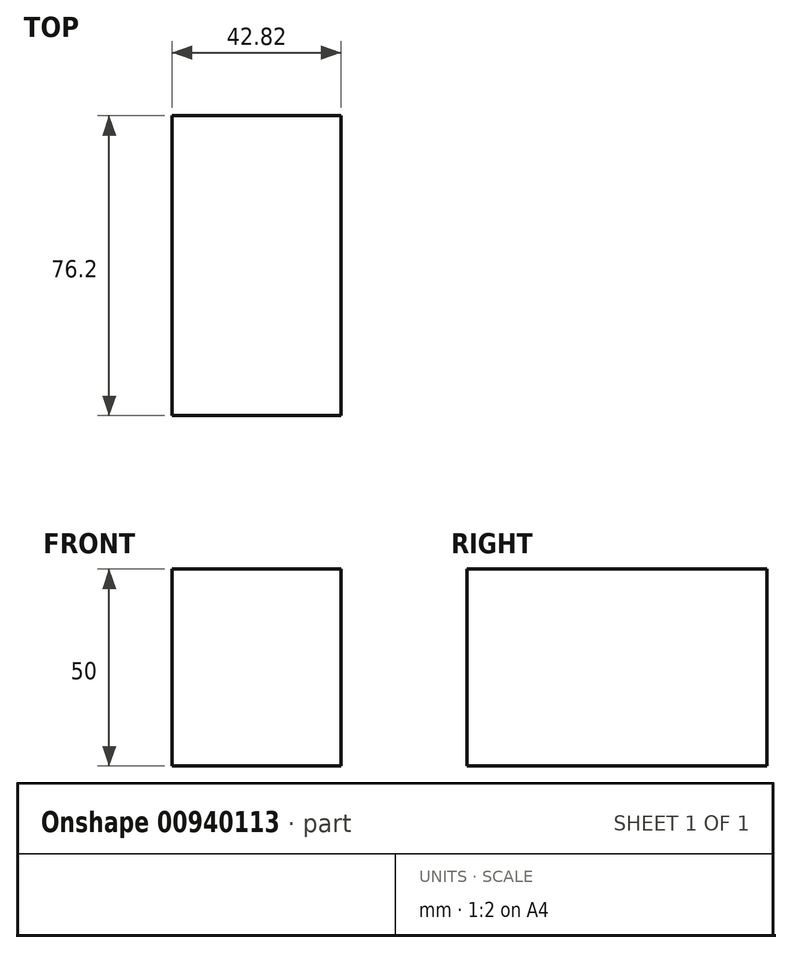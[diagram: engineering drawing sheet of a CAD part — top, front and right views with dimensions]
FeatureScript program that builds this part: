
annotation { "Feature Type Name" : "Feature", "Feature Type Description" : "" }
export const myFeature = defineFeature(function(context is Context, id is Id, definition is map)
    precondition{}
    {
        {
            var Q0;
            Q0=qCreatedBy(makeId("Front.planeOp"),FACE);
            var sketch = newSketch(context, id + "F0", { "sketchPlane" : qUnion([Q0])});
            skLineSegment(sketch, "E0.bottom", {"start": v(21.4, 25) * mm, "end": v(-21.4, 25) * mm});
            skLineSegment(sketch, "E0.top", {"start": v(21.4, -25) * mm, "end": v(-21.4, -25) * mm});
            skLineSegment(sketch, "E0.left", {"start": v(21.4, 25) * mm, "end": v(21.4, -25) * mm});
            skLineSegment(sketch, "E0.right", {"start": v(-21.4, 25) * mm, "end": v(-21.4, -25) * mm});
            skPoint(sketch, "E0.middle", {"position": v(0, 0) * mm});
            skSolve(sketch);
        }
        {
            var Q0;
            Q0=makeQuery(id+"F0.imprint","IMPRINT",FACE,{"disambiguationData":[TD([[makeQuery(id+"F0.imprint","IMPRINT",EDGE,{"derivedFrom":sQuery(id+"F0.wireOp",EDGE,"E0.bottom")}),1.0]])]});
            extrude(context, id + "F1", {"entities" : qUnion([Q0]), "depth" : 76.2 * mm, "offsetDistance" : 25.4 * mm});
        }
    });
